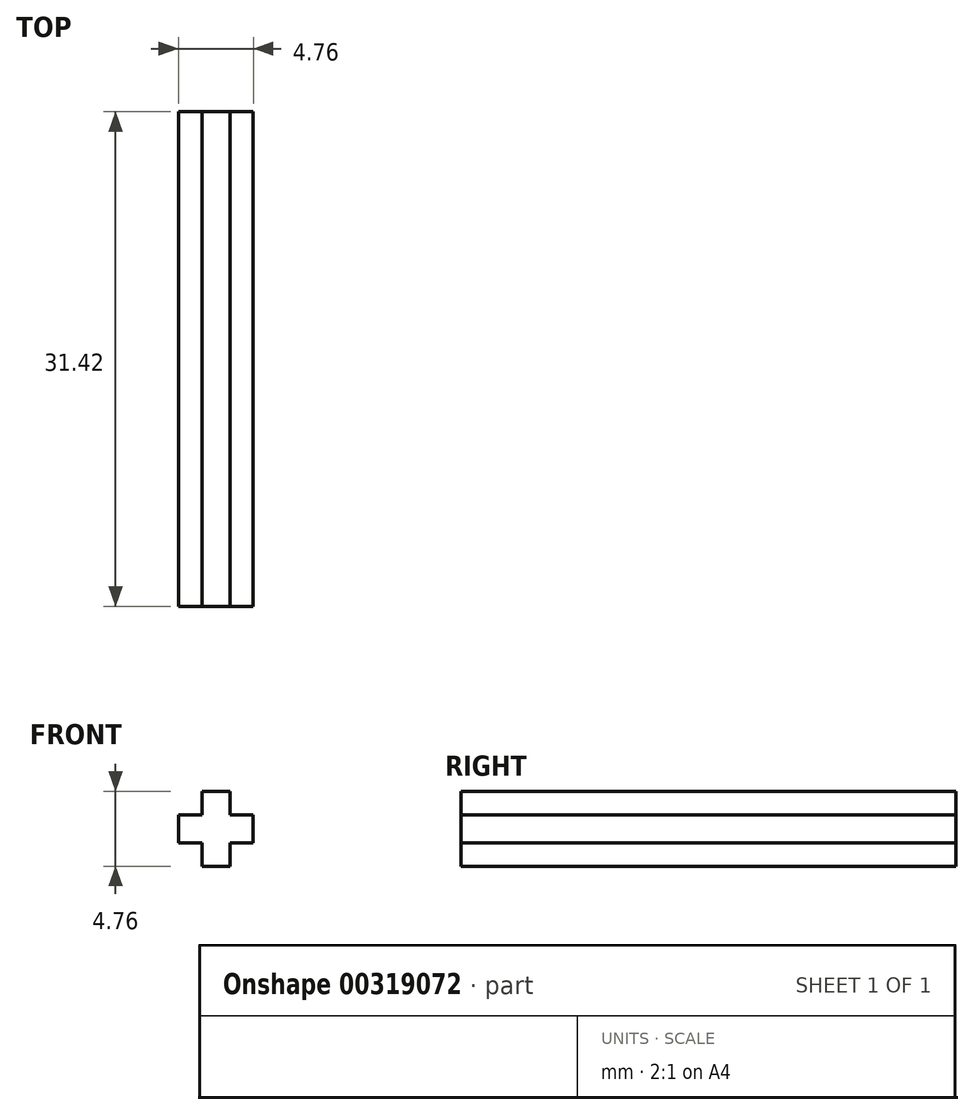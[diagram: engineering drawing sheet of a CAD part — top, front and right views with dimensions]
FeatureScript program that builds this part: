
annotation { "Feature Type Name" : "Feature", "Feature Type Description" : "" }
export const myFeature = defineFeature(function(context is Context, id is Id, definition is map)
    precondition{}
    {
        {
            var Q0;
            Q0=qCreatedBy(makeId("Front.planeOp"),FACE);
            var sketch = newSketch(context, id + "F0", { "sketchPlane" : qUnion([Q0])});
            skLineSegment(sketch, "E0.bottom", {"start": v(-2.38, 0.89) * mm, "end": v(2.38, 0.89) * mm});
            skLineSegment(sketch, "E0.top", {"start": v(-2.38, -0.89) * mm, "end": v(2.38, -0.9) * mm});
            skLineSegment(sketch, "E0.left", {"start": v(-2.38, 0.9) * mm, "end": v(-2.38, -0.9) * mm});
            skLineSegment(sketch, "E0.right", {"start": v(2.38, 0.9) * mm, "end": v(2.38, -0.9) * mm});
            skLineSegment(sketch, "E1.bottom", {"start": v(-0.9, 2.38) * mm, "end": v(0.9, 2.38) * mm});
            skLineSegment(sketch, "E1.top", {"start": v(-0.9, -2.37) * mm, "end": v(0.9, -2.37) * mm});
            skLineSegment(sketch, "E1.left", {"start": v(-0.9, 2.37) * mm, "end": v(-0.9, -2.37) * mm});
            skLineSegment(sketch, "E1.right", {"start": v(0.89, 2.37) * mm, "end": v(0.89, -2.37) * mm});
            skLineSegment(sketch, "E2", {"start": v(0, -0.9) * mm, "end": v(0, 0.9) * mm});
            skLineSegment(sketch, "E3", {"start": v(-0.9, 0) * mm, "end": v(0.9, 0) * mm});
            skPoint(sketch, "E4", {"position": v(0, 0) * mm});
            skSolve(sketch);
        }
        {
            var Q0;
            Q0=qSketchRegion(id+"F0",true);
            extrude(context, id + "F1", {"entities" : qUnion([Q0]), "endBound" : BoundingType.SYMMETRIC, "depth" : 31.41 * mm});
        }
    });
